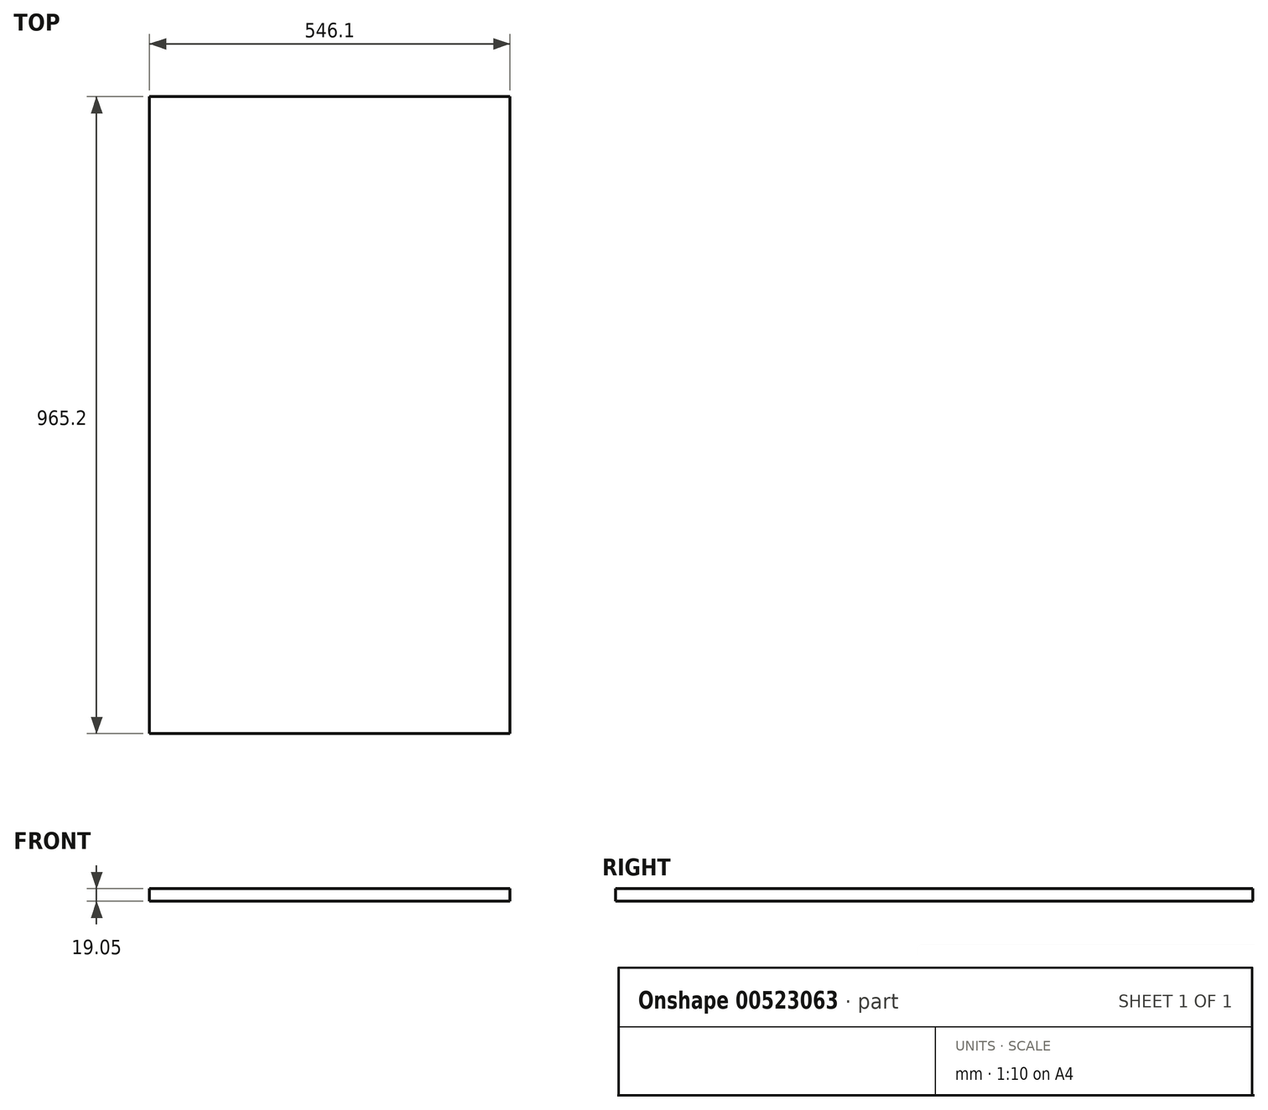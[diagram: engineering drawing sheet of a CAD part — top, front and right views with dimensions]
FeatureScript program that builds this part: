
annotation { "Feature Type Name" : "Feature", "Feature Type Description" : "" }
export const myFeature = defineFeature(function(context is Context, id is Id, definition is map)
    precondition{}
    {
        {
            var Q0;
            Q0=qCreatedBy(makeId("Top.planeOp"),FACE);
            var sketch = newSketch(context, id + "F0", { "sketchPlane" : qUnion([Q0])});
            skLineSegment(sketch, "E0.bottom", {"start": v(0, 0) * mm, "end": v(546.1, 0) * mm});
            skLineSegment(sketch, "E0.top", {"start": v(0, 965.2) * mm, "end": v(546.1, 965.2) * mm});
            skLineSegment(sketch, "E0.left", {"start": v(0, 0) * mm, "end": v(0, 965.2) * mm});
            skLineSegment(sketch, "E0.right", {"start": v(546.1, 0) * mm, "end": v(546.1, 965.2) * mm});
            skSolve(sketch);
        }
        {
            var Q0;
            Q0 = qSketchRegion(id + "F0", true);
            extrude(context, id + "F1", {"entities" : qUnion([Q0]), "depth" : 19.05 * mm, "offsetDistance" : 25.4 * mm});
        }
    });
